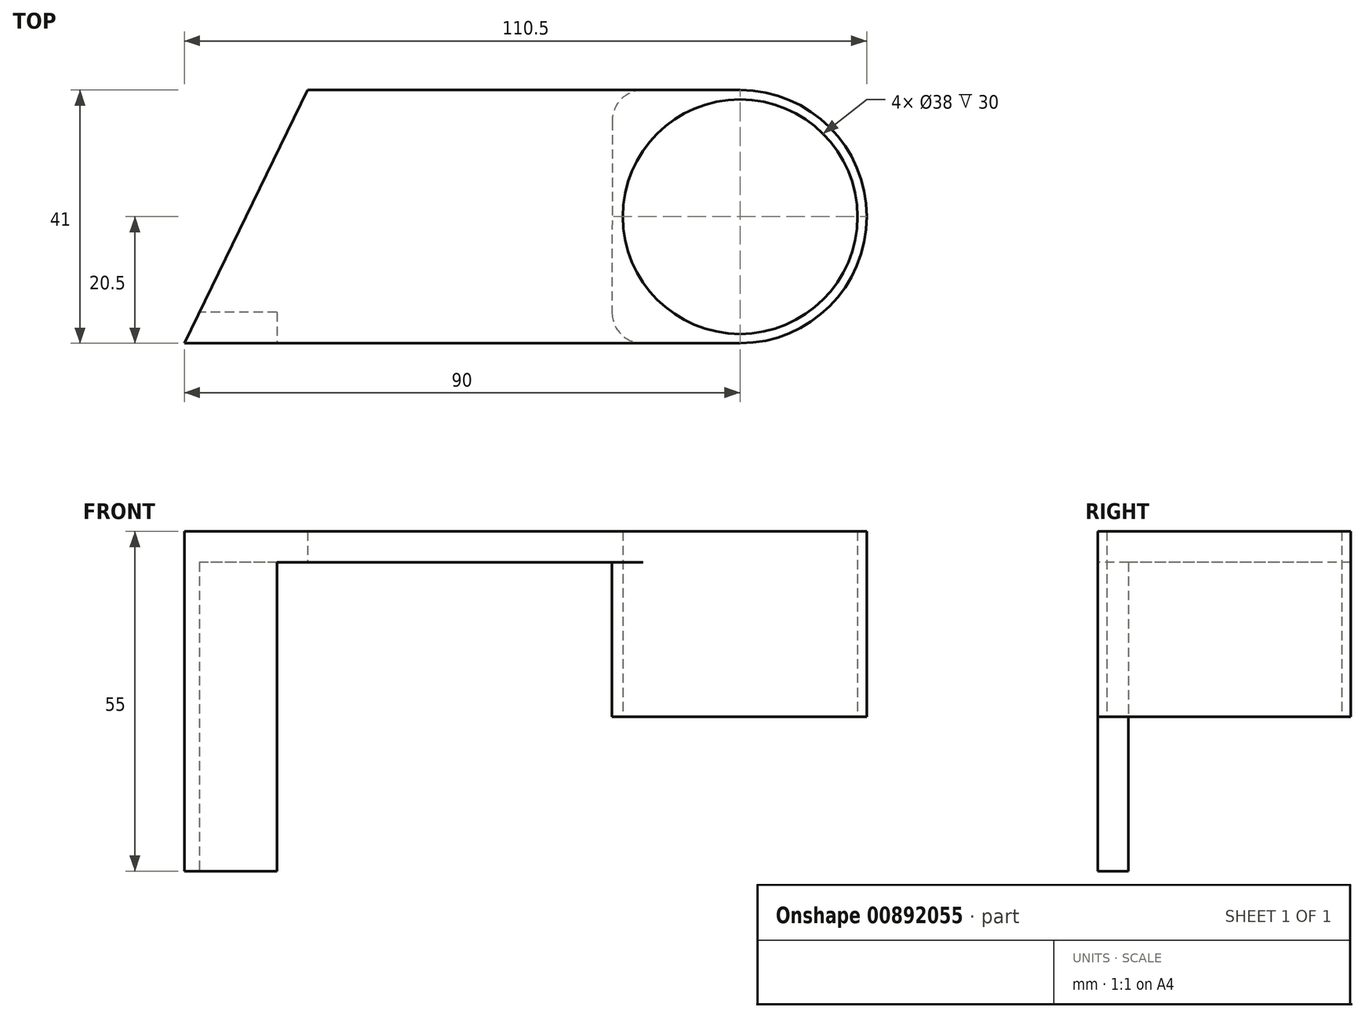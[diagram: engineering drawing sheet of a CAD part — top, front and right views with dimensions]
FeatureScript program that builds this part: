
annotation { "Feature Type Name" : "Feature", "Feature Type Description" : "" }
export const myFeature = defineFeature(function(context is Context, id is Id, definition is map)
    precondition{}
    {
        {
            var Q0;
            Q0=qCreatedBy(makeId("Top.planeOp"),FACE);
            var sketch = newSketch(context, id + "F0", { "sketchPlane" : qUnion([Q0])});
            skCircle(sketch, "E0", {"center": v(0, 0) * mm, "radius": 20.5 * mm});
            skCircle(sketch, "E1", {"center": v(0, 0) * mm, "radius": 19 * mm});
            skLineSegment(sketch, "E2", {"start": v(0, 0) * mm, "end": v(0, 20.5) * mm});
            skLineSegment(sketch, "E3", {"start": v(0, 20.5) * mm, "end": v(-70, 20.5) * mm});
            skLineSegment(sketch, "E4", {"start": v(0, -20.5) * mm, "end": v(-90, -20.5) * mm});
            skLineSegment(sketch, "E5", {"start": v(-70, 20.5) * mm, "end": v(-90, -20.5) * mm});
            skSolve(sketch);
        }
        {
            var Q0;
            Q0 = qSketchRegion(id + "F0", true);
            extrude(context, id + "F1", {"entities" : qUnion([Q0]), "depth" : 55 * mm, "offsetDistance" : 25 * mm});
        }
        {
            var Q0;
            {var subQ0=sQuery(id+"F0.wireOp",EDGE,"E3");Q0=makeQuery(id+"F0.imprint","IMPRINT",FACE,{"disambiguationData":[TD([[makeQuery(id+"F0.imprint","IMPRINT",EDGE,{"derivedFrom":subQ0}),1.0]])]});}
            var sketch = newSketch(context, id + "F2", { "sketchPlane" : qUnion([Q0])});
            skLineSegment(sketch, "E6", {"start": v(-92.3, 24.13) * mm, "end": v(-20.7, 24.13) * mm});
            skLineSegment(sketch, "E7", {"start": v(-75, -15.5) * mm, "end": v(-92.68, -15.5) * mm});
            skLineSegment(sketch, "E8", {"start": v(-92.68, -15.5) * mm, "end": v(-92.3, 24.13) * mm});
            skLineSegment(sketch, "E9", {"start": v(-75, -15.5) * mm, "end": v(-75, -22) * mm});
            skLineSegment(sketch, "E10", {"start": v(-75, -22) * mm, "end": v(-20.75, -22) * mm});
            skLineSegment(sketch, "E11", {"start": v(-20.7, 24.13) * mm, "end": v(-20.75, -22) * mm});
            skSolve(sketch);
        }
        {
            var Q0;
            Q0 = qSketchRegion(id + "F2", true);
            extrude(context, id + "F3", {"entities" : qUnion([Q0]), "operationType" : NewBodyOperationType.REMOVE, "depth" : 50 * mm, "offsetDistance" : 25 * mm});
        }
        {
            var Q0;
            {var subQ0=sQuery(id+"F2.wireOp",EDGE,"E11");var subQ1=sQuery(id+"F0.wireOp",EDGE,"E3");var subQ2=makeQuery(id+"F0.imprint","IMPRINT",EDGE,{"derivedFrom":subQ1});var subQ3=makeQuery(id+"F2.imprint","INTERSECT",VERTEX,{"derivedFrom":[subQ2,subQ0]});Q0=makeQuery(id+"F2.imprint","IMPRINT",FACE,{"disambiguationData":[TD([[makeQuery(id+"F2.imprint","IMPRINT",EDGE,{"disambiguationData":[TD([[subQ3,-1.0]])],"derivedFrom":subQ0}),1.0]])]});}
            var sketch = newSketch(context, id + "F4", { "sketchPlane" : qUnion([Q0])});
            skLineSegment(sketch, "E12.bottom", {"start": v(-24.09, -27.18) * mm, "end": v(22.58, -27.18) * mm});
            skLineSegment(sketch, "E12.top", {"start": v(-24.09, 30.66) * mm, "end": v(22.58, 30.66) * mm});
            skLineSegment(sketch, "E12.left", {"start": v(-24.09, -27.18) * mm, "end": v(-24.09, 30.66) * mm});
            skLineSegment(sketch, "E12.right", {"start": v(22.58, -27.18) * mm, "end": v(22.58, 30.66) * mm});
            skSolve(sketch);
        }
        {
            var Q0;
            Q0 = qSketchRegion(id + "F4", true);
            extrude(context, id + "F5", {"entities" : qUnion([Q0]), "operationType" : NewBodyOperationType.REMOVE, "depth" : 25 * mm, "offsetDistance" : 25 * mm});
        }
        {
            var Q0;
            Q0=makeQuery(id+"F3.boolean.opBoolean","INTERSECT",EDGE,{"derivedFrom":[makeQuery(id+"F1.opExtrude","SWEPT_FACE",FACE,{"disambiguationData":[OSD([sQuery(id+"F0.wireOp",EDGE,"E3")])]}),makeQuery(id+"F3.opExtrude","SWEPT_FACE",FACE,{"disambiguationData":[OSD([sQuery(id+"F2.wireOp",EDGE,"E11")])]})]});
            var Q1;
            Q1=makeQuery(id+"F3.boolean.opBoolean","INTERSECT",EDGE,{"derivedFrom":[makeQuery(id+"F1.opExtrude","SWEPT_FACE",FACE,{"disambiguationData":[OSD([sQuery(id+"F0.wireOp",EDGE,"E4")])]}),makeQuery(id+"F3.opExtrude","SWEPT_FACE",FACE,{"disambiguationData":[OSD([sQuery(id+"F2.wireOp",EDGE,"E11")])]})]});
            fillet(context, id + "F6", {"entities" : qUnion([Q0, Q1]), "radius" : 5 * mm, "tangentPropagation" : true, "allowEdgeOverflow" : false});
        }
    });
